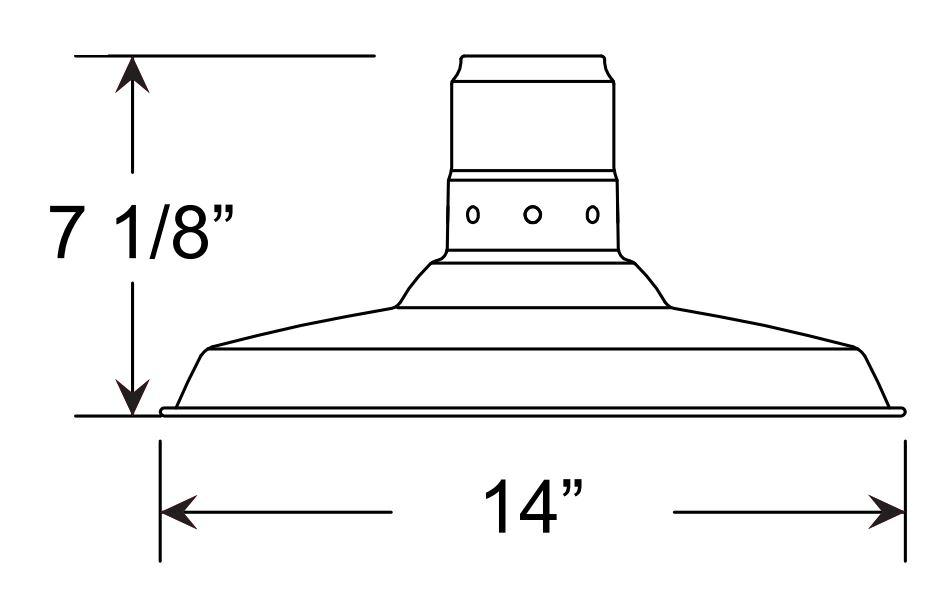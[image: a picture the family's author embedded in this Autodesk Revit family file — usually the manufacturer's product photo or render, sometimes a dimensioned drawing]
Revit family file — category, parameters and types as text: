
# Revit family: Warehoouse_SB_LED
name_source: partatom
category: Lighting Fixtures
units: mm (PartAtom-declared; Revit-internal decimal feet)

## family parameters
Always vertical = Yes
Cut with Voids When Loaded = No
Light Source = Yes
OmniClass Number = 23.80.70.00
OmniClass Title = Lighting
Part Type = Normal
Room Calculation Point = No
Round Connector Dimension = Use Diameter
Shared = No
Work Plane-Based = No

## types (3) — shared parameters
Body Colour = Spun aluminium
Body Material = body
Bulb = BULB
CRI = >90
Color Filter = 16777215
Construction Material = Heavy Duty spun aluminum.
Default Elevation = 0' - 0"
Description = 120-277 Voltage
Dimming = 1%
Dimming Lamp Color Temperature Shift = <None>
Efficiency = 65-125 lumens per watt
GLASS = Glass
Inside body material = INSIDE BODY MATERIAL
Lamp = LED
Life = L70 50,000 hours
Load Classification = Lighting
Manufacturer = ANP Lighting
Power Factor = 1
Tilt Angle = 90.00°
URL = https://www.anplighting.com
Voltage = 277 V
Warranty = 5 year limited warranty

## per-type parameters (varying)
| type | Apparent Load | Fixture Diameter | Fixture Height | Photometric Web File | SBW16 | SBW18 | SBW20 | Wattage Comments | Weight |
| SBW16 | 24 VA | 1' - 4" | 1' - 0" | SBW16M024LDDW40K.IES | Yes | No | No | 24W | 3.0 lb |
| SBW18 | 16 VA | 1' - 6 1/2" | 1' - 2" | SBW18M016LDDW40K.IES | No | Yes | No | 16W | 3.0 lb |
| SBW20 | 24 VA | 1' - 8" | 1' - 3 1/2" | SBW20M024LDDW40K.IES | No | No | Yes | 24W | 4.0 lb |

note: column(s) folded — value = type name in every type: Model

## geometry (parser evidence)
native form markers: Sweep x32
no freeform markers — native parametric forms only
